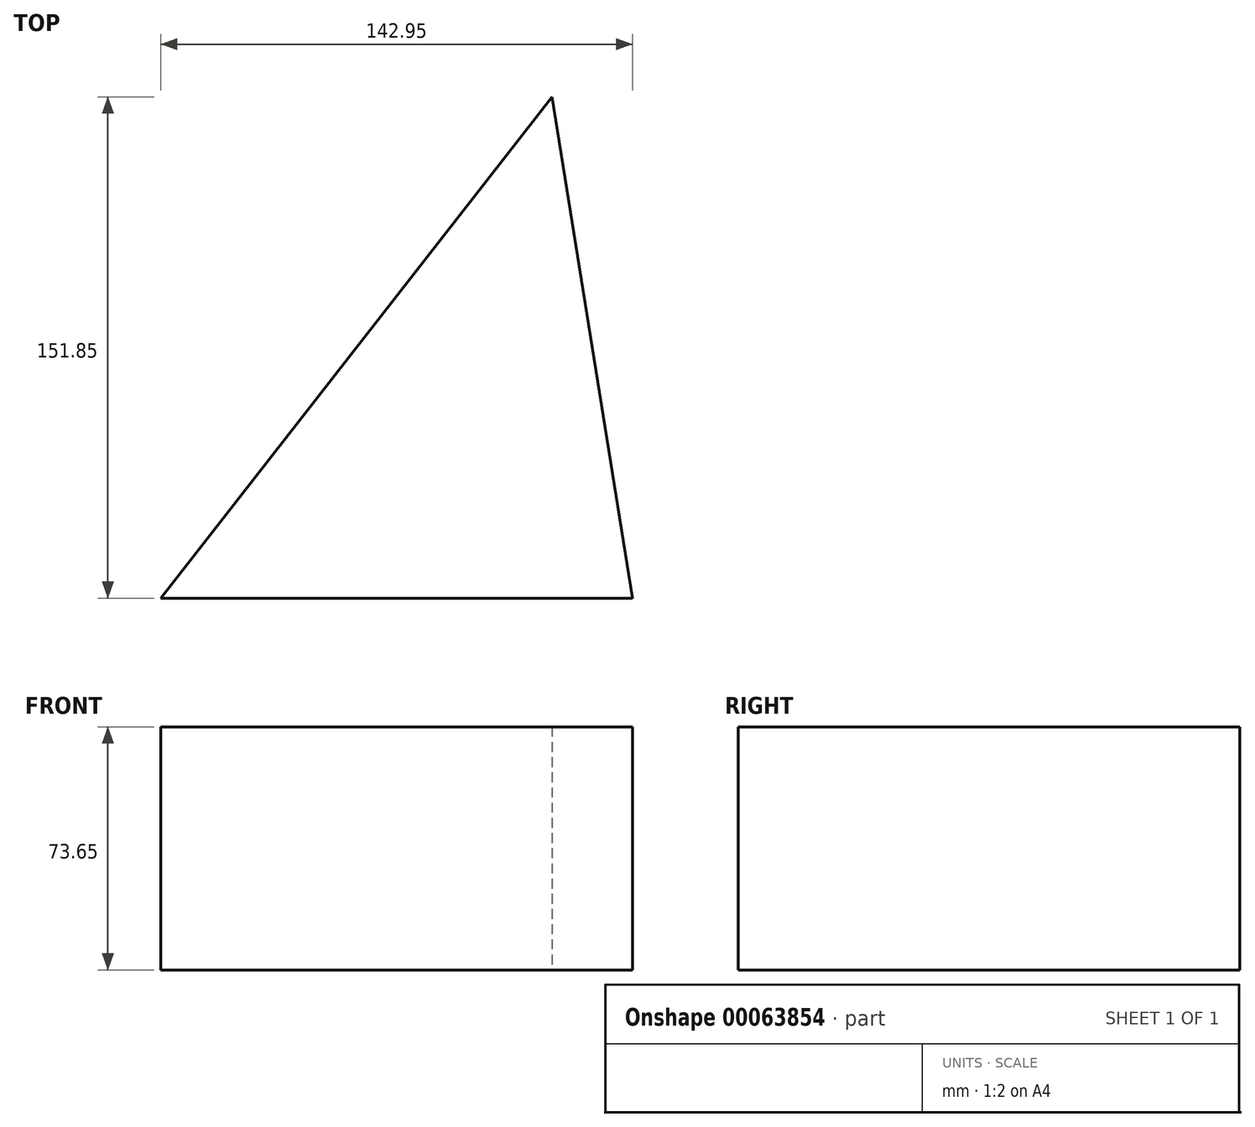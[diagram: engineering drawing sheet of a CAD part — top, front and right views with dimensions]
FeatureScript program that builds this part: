
annotation { "Feature Type Name" : "Feature", "Feature Type Description" : "" }
export const myFeature = defineFeature(function(context is Context, id is Id, definition is map)
    precondition{}
    {
        {
            var Q0;
            Q0=qCreatedBy(makeId("Top.planeOp"),FACE);
            var sketch = newSketch(context, id + "F0", { "sketchPlane" : qUnion([Q0])});
            skLineSegment(sketch, "E0", {"start": v(0, 0) * mm, "end": v(-24.4, 151.85) * mm});
            skLineSegment(sketch, "E1", {"start": v(-24.4, 151.85) * mm, "end": v(-142.95, 0) * mm});
            skLineSegment(sketch, "E2", {"start": v(0, 0) * mm, "end": v(-142.95, 0) * mm});
            skSolve(sketch);
        }
        {
            var Q0;
            Q0=makeQuery(id+"F0.imprint","IMPRINT",FACE,{"disambiguationData":[TD([[makeQuery(id+"F0.imprint","IMPRINT",EDGE,{"derivedFrom":sQuery(id+"F0.wireOp",EDGE,"E0")}),1.0]])]});
            extrude(context, id + "F1", {"entities" : qUnion([Q0]), "depth" : 73.65 * mm});
        }
    });
